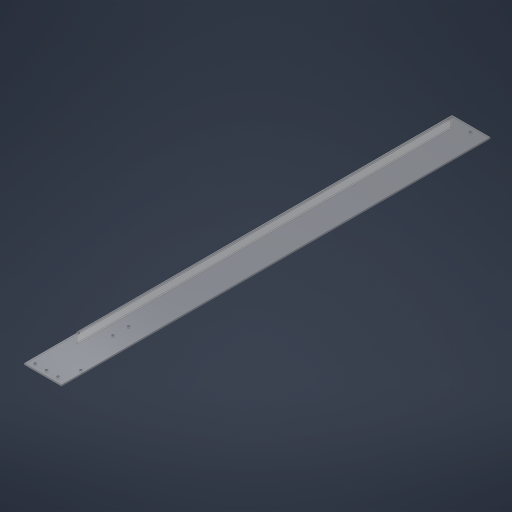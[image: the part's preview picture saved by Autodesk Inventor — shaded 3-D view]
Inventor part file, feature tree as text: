
AUTODESK INVENTOR PART (.ipt)
format: ipt  version: 2023.4 (Build 274418000, 418)  size: 263,680 bytes
history: native  units: in
note: dims shown in document units (in); Inventor stores cm internally (conversion verified against a paired STEP export)
features: sheet_metal_op x4, sketch x3, hole x2, other x2, extrude x1, projected_geometry x1
ambient origin geometry x8: Origin, YZ Plane, XZ Plane, XY Plane, X Axis, Y Axis, Z Axis, Center Point
bodies: Solid1 (feature_tree)
feature tree (13):
  sketch  "Sketch1"  dims[d1=1.5in d2=3.5in]
  sheet_metal_op  "Face1"
  hole  "Hole1"  [1 undecoded]
  hole  "Hole2"  [1 undecoded]
  extrude  "Extrusion1"  Depth=0.125in
  sheet_metal_op  "Flange1"
  other  "Plate1"
  sketch  "Sketch2"  dims[d3=39.375in d4=0.5in]
  sketch  "Sketch3"  dims[d5=5.0in d6=0.5in d7=1.0in d8=1.0in d9=1.375in d10=0.3125in d11=3.1875in d12=3.0in d13=0.25in d14=0.125in d15=0.5in d16=2.5in d17=0.375in d18=37.5in d19=0.17in d20=0.17in d21=0.1in d23=0.201in d26=0.125in d27=0.125in d28=3.5in d29=0.275in d31=0.125in d32=0.201in d33=0.75in d34=0.385in d35=0.25in d36=0.5635in d37=0.125in d38=0.8108in d39=1.375in d40=0.52in d41=0.52in d42=0.52in d43=1.7933in d44=1.345in d45=3.26in d46=1.145in d48=6.0in d49=0.201in d50=0.75in d51=0.375in d52=0.25in d53=0.5635in d54=1.0in d55=0.8108in d56=6.0in d58=0.5in d59=0.0in d60=0.0in d61=2.0in d62=0.125in d63=0.0625in d64=0.25in d65=0.125in d66=1.0in d67=90.0deg d68=0.125in d69=0.5in d70=0.125in d71=0.125in]
  other  "Plate2"
  sheet_metal_op  "Bend1"
  sheet_metal_op  "Corner1"
  projected_geometry  "Project Cut Edges1"
note: 2 required parameter values undecoded (feature->parameter linkage not recoverable at this tier; creation-order binding heuristic only, values carry confidence <= 0.55)
